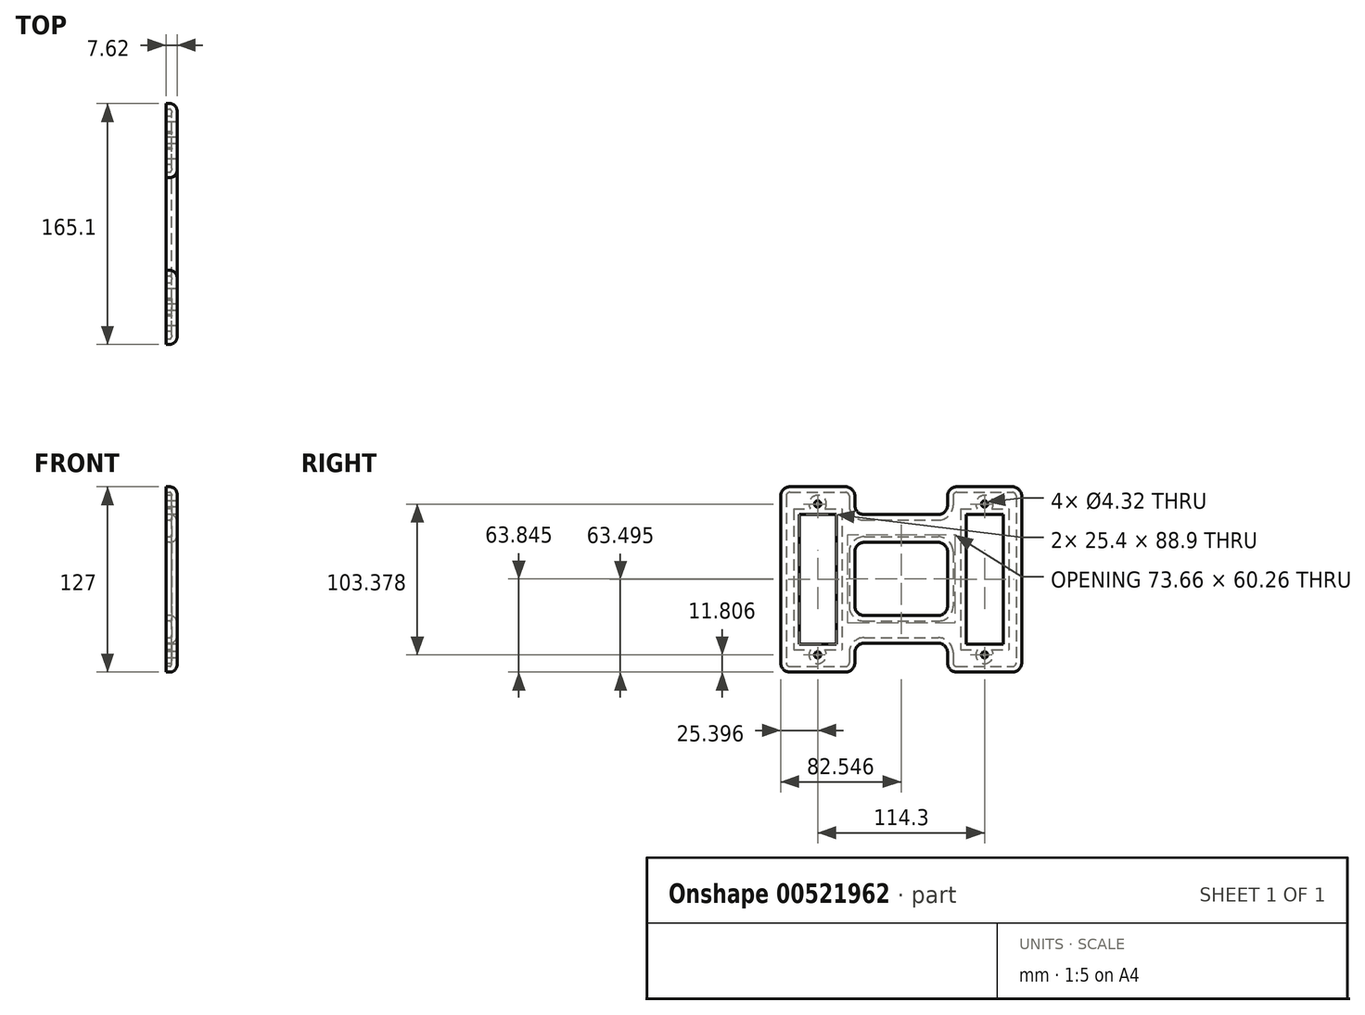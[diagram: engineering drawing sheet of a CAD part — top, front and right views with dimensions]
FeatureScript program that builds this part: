
annotation { "Feature Type Name" : "Feature", "Feature Type Description" : "" }
export const myFeature = defineFeature(function(context is Context, id is Id, definition is map)
    precondition{}
    {
        {
            var Q0;
            Q0=qCreatedBy(makeId("Right.planeOp"),FACE);
            var sketch = newSketch(context, id + "F0", { "sketchPlane" : qUnion([Q0])});
            skLineSegment(sketch, "E0.bottom", {"start": v(-74.65, 94.95) * mm, "end": v(-36.55, 94.95) * mm});
            skLineSegment(sketch, "E0.top", {"start": v(-74.65, -32.05) * mm, "end": v(-36.55, -32.05) * mm});
            skLineSegment(sketch, "E0.left", {"start": v(-81, 88.6) * mm, "end": v(-81, -25.7) * mm});
            skLineSegment(sketch, "E0.right", {"start": v(-30.2, 88.6) * mm, "end": v(-30.2, 82.25) * mm});
            skLineSegment(sketch, "E1.bottom", {"start": v(39.65, 94.95) * mm, "end": v(77.75, 94.95) * mm});
            skLineSegment(sketch, "E1.top", {"start": v(39.65, -32.05) * mm, "end": v(77.75, -32.05) * mm});
            skLineSegment(sketch, "E1.left", {"start": v(33.3, 88.6) * mm, "end": v(33.3, 82.25) * mm});
            skLineSegment(sketch, "E1.right", {"start": v(84.1, 88.6) * mm, "end": v(84.1, -25.7) * mm});
            skLineSegment(sketch, "E2.bottom", {"start": v(-68.3, 75.9) * mm, "end": v(-42.9, 75.9) * mm});
            skLineSegment(sketch, "E2.top", {"start": v(-68.3, -13) * mm, "end": v(-42.9, -13) * mm});
            skLineSegment(sketch, "E2.left", {"start": v(-68.3, 75.9) * mm, "end": v(-68.3, -13) * mm});
            skLineSegment(sketch, "E2.right", {"start": v(-42.9, 75.9) * mm, "end": v(-42.9, -13) * mm});
            skLineSegment(sketch, "E3.bottom", {"start": v(46, 75.9) * mm, "end": v(71.4, 75.9) * mm});
            skLineSegment(sketch, "E3.top", {"start": v(46, -13) * mm, "end": v(71.4, -13) * mm});
            skLineSegment(sketch, "E3.left", {"start": v(46, 75.9) * mm, "end": v(46, -13) * mm});
            skLineSegment(sketch, "E3.right", {"start": v(71.4, 75.9) * mm, "end": v(71.4, -13) * mm});
            skLineSegment(sketch, "E4.bottom", {"start": v(-23.85, -12.3) * mm, "end": v(26.95, -12.3) * mm});
            skLineSegment(sketch, "E4.top", {"start": v(-23.85, 6.75) * mm, "end": v(26.95, 6.75) * mm});
            skLineSegment(sketch, "E5.bottom", {"start": v(-23.85, 75.9) * mm, "end": v(26.95, 75.9) * mm});
            skLineSegment(sketch, "E5.top", {"start": v(-23.85, 56.85) * mm, "end": v(26.95, 56.85) * mm});
            skLineSegment(sketch, "E6.trimOffspring", {"start": v(-30.2, 50.5) * mm, "end": v(-30.2, 13.1) * mm});
            skLineSegment(sketch, "E7.trimOffspring", {"start": v(33.3, -18.65) * mm, "end": v(33.3, -25.7) * mm});
            skLineSegment(sketch, "E8.trimOffspring", {"start": v(33.3, 50.5) * mm, "end": v(33.3, 13.1) * mm});
            skLineSegment(sketch, "E9.trimOffspring", {"start": v(-30.2, -18.65) * mm, "end": v(-30.2, -25.7) * mm});
            skPoint(sketch, "E10.visualSharp", {"position": v(-30.2, 56.85) * mm});
            skArc(sketch, "E10.filletArc", {"start": v(-23.85, 56.85) * mm, "mid": v(-28.34, 54.99) * mm, "end": v(-30.2, 50.5) * mm});
            skPoint(sketch, "E11.visualSharp", {"position": v(-30.2, 6.75) * mm});
            skArc(sketch, "E11.filletArc", {"start": v(-30.2, 13.1) * mm, "mid": v(-28.34, 8.6) * mm, "end": v(-23.85, 6.75) * mm});
            skPoint(sketch, "E12.visualSharp", {"position": v(33.3, 6.75) * mm});
            skArc(sketch, "E12.filletArc", {"start": v(26.95, 6.75) * mm, "mid": v(31.44, 8.6) * mm, "end": v(33.3, 13.1) * mm});
            skPoint(sketch, "E13.visualSharp", {"position": v(33.3, 56.85) * mm});
            skArc(sketch, "E13.filletArc", {"start": v(33.3, 50.5) * mm, "mid": v(31.44, 54.99) * mm, "end": v(26.95, 56.85) * mm});
            skPoint(sketch, "E14.visualSharp", {"position": v(33.3, 75.9) * mm});
            skArc(sketch, "E14.filletArc", {"start": v(26.95, 75.9) * mm, "mid": v(31.44, 77.75) * mm, "end": v(33.3, 82.25) * mm});
            skPoint(sketch, "E15.visualSharp", {"position": v(-30.2, 75.9) * mm});
            skArc(sketch, "E15.filletArc", {"start": v(-30.2, 82.25) * mm, "mid": v(-28.34, 77.75) * mm, "end": v(-23.85, 75.9) * mm});
            skPoint(sketch, "E16.visualSharp", {"position": v(-30.2, 94.95) * mm});
            skArc(sketch, "E16.filletArc", {"start": v(-30.2, 88.6) * mm, "mid": v(-32.06, 93.09) * mm, "end": v(-36.55, 94.95) * mm});
            skPoint(sketch, "E17.visualSharp", {"position": v(-81, 94.95) * mm});
            skArc(sketch, "E17.filletArc", {"start": v(-74.65, 94.95) * mm, "mid": v(-79.14, 93.09) * mm, "end": v(-81, 88.6) * mm});
            skPoint(sketch, "E18.visualSharp", {"position": v(-81, -32.05) * mm});
            skArc(sketch, "E18.filletArc", {"start": v(-81, -25.7) * mm, "mid": v(-79.14, -30.2) * mm, "end": v(-74.65, -32.05) * mm});
            skPoint(sketch, "E19.visualSharp", {"position": v(-30.2, -32.05) * mm});
            skArc(sketch, "E19.filletArc", {"start": v(-36.55, -32.05) * mm, "mid": v(-32.06, -30.2) * mm, "end": v(-30.2, -25.7) * mm});
            skPoint(sketch, "E20.visualSharp", {"position": v(-30.2, -12.3) * mm});
            skArc(sketch, "E20.filletArc", {"start": v(-23.85, -12.3) * mm, "mid": v(-28.34, -14.16) * mm, "end": v(-30.2, -18.65) * mm});
            skPoint(sketch, "E21.visualSharp", {"position": v(33.3, -12.3) * mm});
            skArc(sketch, "E21.filletArc", {"start": v(33.3, -18.65) * mm, "mid": v(31.44, -14.16) * mm, "end": v(26.95, -12.3) * mm});
            skPoint(sketch, "E22.visualSharp", {"position": v(33.3, -32.05) * mm});
            skArc(sketch, "E22.filletArc", {"start": v(33.3, -25.7) * mm, "mid": v(35.16, -30.2) * mm, "end": v(39.65, -32.05) * mm});
            skPoint(sketch, "E23.visualSharp", {"position": v(84.1, -32.05) * mm});
            skArc(sketch, "E23.filletArc", {"start": v(77.75, -32.05) * mm, "mid": v(82.24, -30.2) * mm, "end": v(84.1, -25.7) * mm});
            skPoint(sketch, "E24.visualSharp", {"position": v(84.1, 94.95) * mm});
            skArc(sketch, "E24.filletArc", {"start": v(84.1, 88.6) * mm, "mid": v(82.24, 93.09) * mm, "end": v(77.75, 94.95) * mm});
            skPoint(sketch, "E25.visualSharp", {"position": v(33.3, 94.95) * mm});
            skArc(sketch, "E25.filletArc", {"start": v(39.65, 94.95) * mm, "mid": v(35.16, 93.09) * mm, "end": v(33.3, 88.6) * mm});
            skCircle(sketch, "E26", {"center": v(-55.6, 83.13) * mm, "radius": 2.16 * mm});
            skPoint(sketch, "E26.centerSnap0", {"position": v(-55.6, 94.95) * mm});
            skCircle(sketch, "E27", {"center": v(58.7, -20.24) * mm, "radius": 2.16 * mm});
            skPoint(sketch, "E27.centerSnap0", {"position": v(58.7, -32.05) * mm});
            skCircle(sketch, "E28", {"center": v(-55.6, -20.24) * mm, "radius": 2.16 * mm});
            skPoint(sketch, "E28.centerSnap0", {"position": v(-55.6, -32.05) * mm});
            skCircle(sketch, "E29", {"center": v(58.7, 83.13) * mm, "radius": 2.16 * mm});
            skPoint(sketch, "E29.centerSnap0", {"position": v(58.7, 94.95) * mm});
            skSolve(sketch);
        }
        {
            var Q0;
            Q0=makeQuery(id+"F0.imprint","IMPRINT",FACE,{"disambiguationData":[TD([[makeQuery(id+"F0.imprint","IMPRINT",EDGE,{"derivedFrom":sQuery(id+"F0.wireOp",EDGE,"E0.bottom")}),-1.0]])]});
            extrude(context, id + "F1", {"entities" : qUnion([Q0]), "depth" : 7.62 * mm, "offsetDistance" : 25.4 * mm});
        }
        {
            var Q0;
            Q0=makeQuery(id+"F1.opExtrude","CAP_EDGE",EDGE,{"disambiguationData":[OSD([sQuery(id+"F0.wireOp",EDGE,"E0.top")])],"isStart":false});
            var Q1;
            Q1=makeQuery(id+"F1.opExtrude","CAP_EDGE",EDGE,{"disambiguationData":[OSD([sQuery(id+"F0.wireOp",EDGE,"E5.top")])],"isStart":false});
            fillet(context, id + "F2", {"entities" : qUnion([Q0, Q1]), "radius" : 5.08 * mm, "tangentPropagation" : true, "allowEdgeOverflow" : false});
        }
        {
            var Q0;
            Q0=makeQuery(id+"F1.opExtrude","CAP_FACE",FACE,{"disambiguationData":[OSD([sQuery(id+"F0.wireOp",EDGE,"E0.bottom"),sQuery(id+"F0.wireOp",EDGE,"E0.top"),sQuery(id+"F0.wireOp",EDGE,"E0.left"),sQuery(id+"F0.wireOp",EDGE,"E0.right"),sQuery(id+"F0.wireOp",EDGE,"E1.bottom"),sQuery(id+"F0.wireOp",EDGE,"E1.top"),sQuery(id+"F0.wireOp",EDGE,"E1.left"),sQuery(id+"F0.wireOp",EDGE,"E1.right"),sQuery(id+"F0.wireOp",EDGE,"E2.bottom"),sQuery(id+"F0.wireOp",EDGE,"E2.top"),sQuery(id+"F0.wireOp",EDGE,"E2.left"),sQuery(id+"F0.wireOp",EDGE,"E2.right"),sQuery(id+"F0.wireOp",EDGE,"E3.bottom"),sQuery(id+"F0.wireOp",EDGE,"E3.top"),sQuery(id+"F0.wireOp",EDGE,"E3.left"),sQuery(id+"F0.wireOp",EDGE,"E3.right"),sQuery(id+"F0.wireOp",EDGE,"E4.bottom"),sQuery(id+"F0.wireOp",EDGE,"E4.top"),sQuery(id+"F0.wireOp",EDGE,"E5.bottom"),sQuery(id+"F0.wireOp",EDGE,"E5.top"),sQuery(id+"F0.wireOp",EDGE,"E6.trimOffspring"),sQuery(id+"F0.wireOp",EDGE,"E7.trimOffspring"),sQuery(id+"F0.wireOp",EDGE,"E8.trimOffspring"),sQuery(id+"F0.wireOp",EDGE,"E9.trimOffspring"),sQuery(id+"F0.wireOp",EDGE,"E10.filletArc"),sQuery(id+"F0.wireOp",EDGE,"E11.filletArc"),sQuery(id+"F0.wireOp",EDGE,"E12.filletArc"),sQuery(id+"F0.wireOp",EDGE,"E13.filletArc"),sQuery(id+"F0.wireOp",EDGE,"E14.filletArc"),sQuery(id+"F0.wireOp",EDGE,"E15.filletArc"),sQuery(id+"F0.wireOp",EDGE,"E16.filletArc"),sQuery(id+"F0.wireOp",EDGE,"E17.filletArc"),sQuery(id+"F0.wireOp",EDGE,"E18.filletArc"),sQuery(id+"F0.wireOp",EDGE,"E19.filletArc"),sQuery(id+"F0.wireOp",EDGE,"E20.filletArc"),sQuery(id+"F0.wireOp",EDGE,"E21.filletArc"),sQuery(id+"F0.wireOp",EDGE,"E22.filletArc"),sQuery(id+"F0.wireOp",EDGE,"E23.filletArc"),sQuery(id+"F0.wireOp",EDGE,"E24.filletArc"),sQuery(id+"F0.wireOp",EDGE,"E25.filletArc")])],"isStart":true});
            shell(context, id + "F3", {"entities" : qUnion([Q0]), "thickness" : 3.8 * mm});
        }
    });
